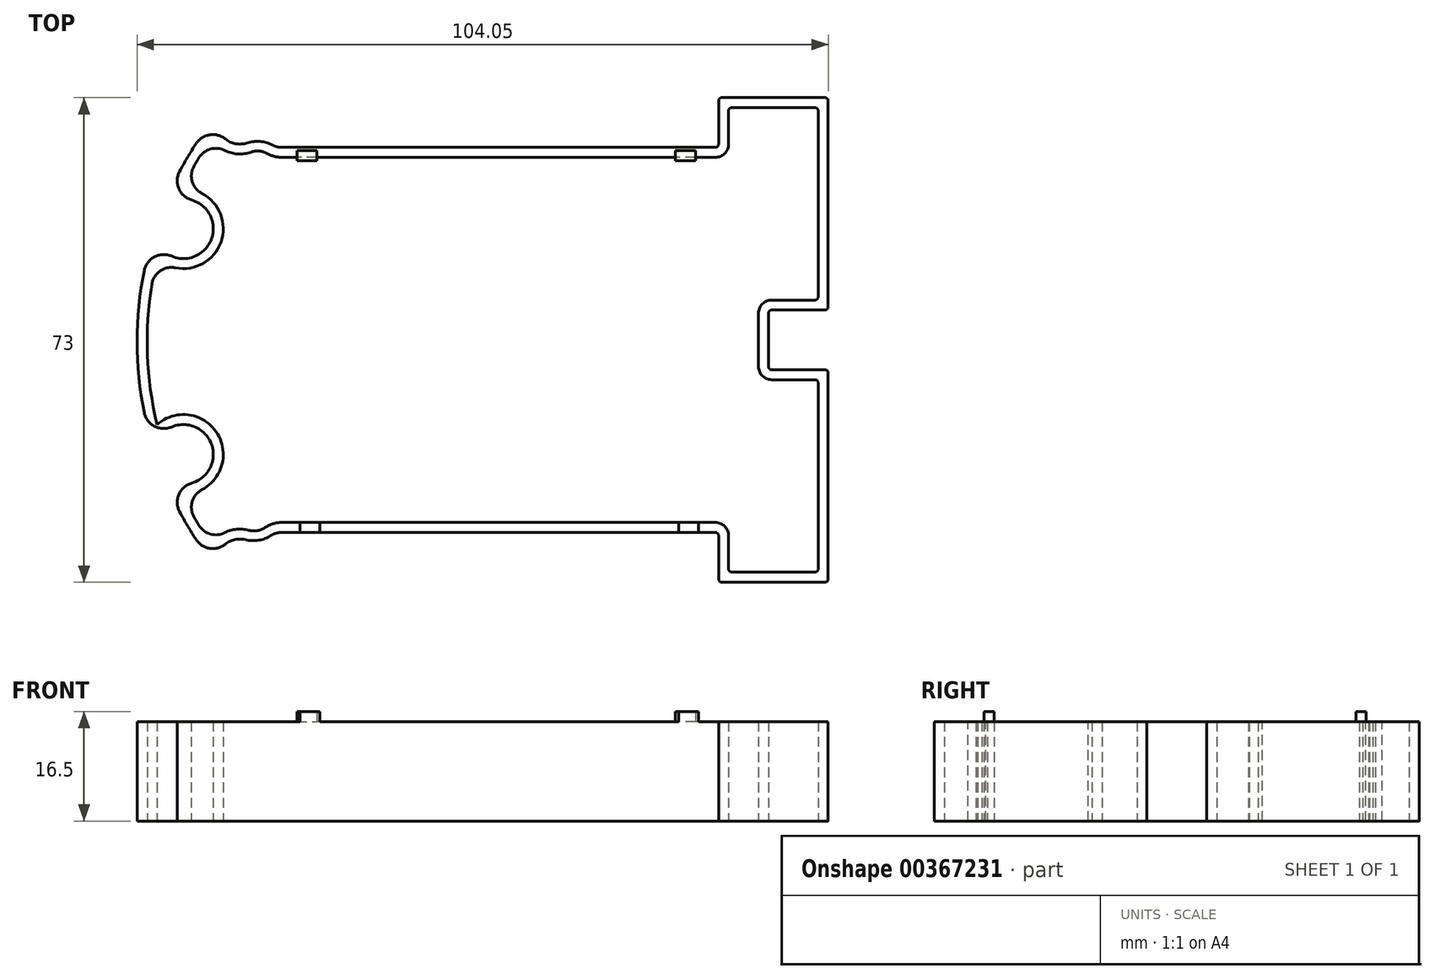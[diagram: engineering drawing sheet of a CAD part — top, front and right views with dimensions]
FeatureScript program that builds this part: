
annotation { "Feature Type Name" : "Feature", "Feature Type Description" : "" }
export const myFeature = defineFeature(function(context is Context, id is Id, definition is map)
    precondition{}
    {
        {
            var Q0;
            Q0=qCreatedBy(makeId("Top.planeOp"),FACE);
            var sketch = newSketch(context, id + "F0", { "sketchPlane" : qUnion([Q0])});
            skLineSegment(sketch, "E0.bottom", {"start": v(50.14, 35.5) * mm, "end": v(34.64, 35.5) * mm});
            skLineSegment(sketch, "E0.top", {"start": v(50.14, -37.5) * mm, "end": v(34.64, -37.5) * mm});
            skLineSegment(sketch, "E0.left", {"start": v(50.64, 35) * mm, "end": v(50.64, 4) * mm});
            skLineSegment(sketch, "E0.right", {"start": v(-53.4, -1.25) * mm, "end": v(-53.4, -1.25) * mm});
            skPoint(sketch, "E0.middle", {"position": v(-1.39, -1.25) * mm});
            skLineSegment(sketch, "E1.0", {"start": v(34.14, 35) * mm, "end": v(34.14, 28.5) * mm});
            skLineSegment(sketch, "E2.0", {"start": v(-34.64, 31) * mm, "end": v(-34.64, 30.87) * mm});
            skLineSegment(sketch, "E3.0", {"start": v(33.64, -30) * mm, "end": v(-31.64, -30) * mm});
            skLineSegment(sketch, "E4.0", {"start": v(33.64, 28) * mm, "end": v(-31.64, 28) * mm});
            skLineSegment(sketch, "E5", {"start": v(-1.39, -1.25) * mm, "end": v(-53.4, -1.25) * mm, "construction": true});
            skArc(sketch, "E6", {"start": v(-41.29, 33.04) * mm, "mid": v(-45.9, 26.36) * mm, "end": v(-49.48, 19.07) * mm});
            skPoint(sketch, "E7.orphan", {"position": v(-53.4, 35) * mm});
            skArc(sketch, "E8.filletArc", {"start": v(-33.03, 28.34) * mm, "mid": v(-32.35, 28.08) * mm, "end": v(-31.64, 28) * mm});
            skLineSegment(sketch, "E9", {"start": v(-34.64, -33.38) * mm, "end": v(-34.64, -33) * mm});
            skPoint(sketch, "E10.visualSharp", {"position": v(-34.64, -30) * mm});
            skArc(sketch, "E10.filletArc", {"start": v(-31.64, -30) * mm, "mid": v(-32.47, -30.12) * mm, "end": v(-33.24, -30.47) * mm});
            skLineSegment(sketch, "E11.trimOffspring", {"start": v(34.14, -30.5) * mm, "end": v(34.14, -37) * mm});
            skPoint(sketch, "E12.visualSharp", {"position": v(34.14, -30) * mm});
            skArc(sketch, "E12.filletArc", {"start": v(34.14, -30.5) * mm, "mid": v(34, -30.15) * mm, "end": v(33.64, -30) * mm});
            skPoint(sketch, "E13.visualSharp", {"position": v(34.14, -37.5) * mm});
            skArc(sketch, "E13.filletArc", {"start": v(34.14, -37) * mm, "mid": v(34.28, -37.36) * mm, "end": v(34.64, -37.5) * mm});
            skPoint(sketch, "E14.visualSharp", {"position": v(50.64, -37.5) * mm});
            skArc(sketch, "E14.filletArc", {"start": v(50.14, -37.5) * mm, "mid": v(50.5, -37.36) * mm, "end": v(50.64, -37) * mm});
            skPoint(sketch, "E15.visualSharp", {"position": v(50.64, 35.5) * mm});
            skArc(sketch, "E15.filletArc", {"start": v(50.64, 35) * mm, "mid": v(50.5, 35.35) * mm, "end": v(50.14, 35.5) * mm});
            skPoint(sketch, "E16.visualSharp", {"position": v(34.14, 35.5) * mm});
            skArc(sketch, "E16.filletArc", {"start": v(34.64, 35.5) * mm, "mid": v(34.28, 35.35) * mm, "end": v(34.14, 35) * mm});
            skPoint(sketch, "E17.visualSharp", {"position": v(34.14, 28) * mm});
            skArc(sketch, "E17.filletArc", {"start": v(33.64, 28) * mm, "mid": v(34, 28.14) * mm, "end": v(34.14, 28.5) * mm});
            skLineSegment(sketch, "E18", {"start": v(-34.64, 30.87) * mm, "end": v(-34.64, 31) * mm});
            skLineSegment(sketch, "E19", {"start": v(1.19, -1.25) * mm, "end": v(50.64, -1) * mm, "construction": true});
            skLineSegment(sketch, "E20.bottom", {"start": v(50.14, 3.5) * mm, "end": v(42.14, 3.5) * mm});
            skLineSegment(sketch, "E20.top", {"start": v(50.14, -5.5) * mm, "end": v(42.14, -5.5) * mm});
            skLineSegment(sketch, "E20.right", {"start": v(41.64, 3) * mm, "end": v(41.64, -5) * mm});
            skLineSegment(sketch, "E21.trimOffspring", {"start": v(50.64, -6) * mm, "end": v(50.64, -37) * mm});
            skLineSegment(sketch, "E22", {"start": v(-37.95, 32) * mm, "end": v(-37.95, -34.5) * mm, "construction": true});
            skArc(sketch, "E23", {"start": v(-41.29, 33.04) * mm, "mid": v(-40.41, 29.51) * mm, "end": v(-36.88, 28.66) * mm});
            skArc(sketch, "E24", {"start": v(-37.11, -31.1) * mm, "mid": v(-40.5, -32.1) * mm, "end": v(-41.29, -35.55) * mm});
            skLineSegment(sketch, "E25.0", {"start": v(-0.88, 15.75) * mm, "end": v(-50.95, 15.75) * mm, "construction": true});
            skLineSegment(sketch, "E26.0", {"start": v(-1.9, -18.25) * mm, "end": v(-53.9, -18.25) * mm, "construction": true});
            skLineSegment(sketch, "E27.0", {"start": v(-46.45, 35) * mm, "end": v(-46.45, -37.5) * mm, "construction": true});
            skArc(sketch, "E28", {"start": v(-50.9, 15.1) * mm, "mid": v(-42.21, 14.23) * mm, "end": v(-49.48, 19.07) * mm});
            skArc(sketch, "E29", {"start": v(-49.48, -21.58) * mm, "mid": v(-42.21, -16.74) * mm, "end": v(-50.9, -17.6) * mm});
            skPoint(sketch, "E30.visualSharp", {"position": v(50.64, -5.5) * mm});
            skArc(sketch, "E30.filletArc", {"start": v(50.64, -6) * mm, "mid": v(50.5, -5.65) * mm, "end": v(50.14, -5.5) * mm});
            skPoint(sketch, "E31.visualSharp", {"position": v(41.64, -5.5) * mm});
            skArc(sketch, "E31.filletArc", {"start": v(41.64, -5) * mm, "mid": v(41.78, -5.36) * mm, "end": v(42.14, -5.5) * mm});
            skPoint(sketch, "E32.visualSharp", {"position": v(41.64, 3.5) * mm});
            skArc(sketch, "E32.filletArc", {"start": v(42.14, 3.5) * mm, "mid": v(41.78, 3.35) * mm, "end": v(41.64, 3) * mm});
            skPoint(sketch, "E33.visualSharp", {"position": v(50.64, 3.5) * mm});
            skArc(sketch, "E33.filletArc", {"start": v(50.14, 3.5) * mm, "mid": v(50.5, 3.64) * mm, "end": v(50.64, 4) * mm});
            skArc(sketch, "E34.0", {"start": v(-31.64, -28.5) * mm, "mid": v(-33.65, -28.98) * mm, "end": v(-35.24, -30.3) * mm});
            skLineSegment(sketch, "E35.0", {"start": v(33.64, -28.5) * mm, "end": v(-31.64, -28.5) * mm});
            skLineSegment(sketch, "E36.0", {"start": v(35.64, -30) * mm, "end": v(35.64, -35.5) * mm});
            skLineSegment(sketch, "E37.0", {"start": v(48.64, -36) * mm, "end": v(36.14, -36) * mm});
            skArc(sketch, "E38.0", {"start": v(35.64, -30.5) * mm, "mid": v(35.05, -29.09) * mm, "end": v(33.64, -28.5) * mm});
            skArc(sketch, "E39.filletArc", {"start": v(35.64, -35.5) * mm, "mid": v(35.78, -35.86) * mm, "end": v(36.14, -36) * mm});
            skLineSegment(sketch, "E40.0", {"start": v(49.14, -7.5) * mm, "end": v(49.14, -35.5) * mm});
            skLineSegment(sketch, "E41.0", {"start": v(49.14, 33.5) * mm, "end": v(49.14, 5.5) * mm});
            skLineSegment(sketch, "E42.0", {"start": v(48.64, 5) * mm, "end": v(42.14, 5) * mm});
            skLineSegment(sketch, "E43.0", {"start": v(40.14, 3) * mm, "end": v(40.14, -5) * mm});
            skLineSegment(sketch, "E44.0", {"start": v(48.64, -7) * mm, "end": v(42.14, -7) * mm});
            skArc(sketch, "E45.0", {"start": v(42.14, 5) * mm, "mid": v(40.72, 4.41) * mm, "end": v(40.14, 3) * mm});
            skArc(sketch, "E46.0", {"start": v(40.14, -5) * mm, "mid": v(40.72, -6.42) * mm, "end": v(42.14, -7) * mm});
            skArc(sketch, "E47.filletArc", {"start": v(48.64, 5) * mm, "mid": v(49, 5.14) * mm, "end": v(49.14, 5.5) * mm});
            skArc(sketch, "E48.filletArc", {"start": v(49.14, -7.5) * mm, "mid": v(49, -7.15) * mm, "end": v(48.64, -7) * mm});
            skArc(sketch, "E49.filletArc", {"start": v(48.64, -36) * mm, "mid": v(49, -35.86) * mm, "end": v(49.14, -35.5) * mm});
            skLineSegment(sketch, "E50.0", {"start": v(48.64, 34) * mm, "end": v(36.14, 34) * mm});
            skLineSegment(sketch, "E51.0", {"start": v(35.64, 33.5) * mm, "end": v(35.64, 28.5) * mm});
            skLineSegment(sketch, "E52.0", {"start": v(33.64, 26.5) * mm, "end": v(-31.64, 26.5) * mm});
            skArc(sketch, "E53.0", {"start": v(-34.97, 27.98) * mm, "mid": v(-33.46, 26.88) * mm, "end": v(-31.64, 26.5) * mm});
            skArc(sketch, "E54.0", {"start": v(-42.2, 29.36) * mm, "mid": v(-38.89, 27.08) * mm, "end": v(-34.97, 27.98) * mm});
            skArc(sketch, "E55.0", {"start": v(-42.2, 29.36) * mm, "mid": v(-44.6, 25.64) * mm, "end": v(-46.67, 21.74) * mm});
            skArc(sketch, "E56.0", {"start": v(-50.42, 11.24) * mm, "mid": v(-40.8, 13.73) * mm, "end": v(-46.67, 21.74) * mm});
            skArc(sketch, "E57.0", {"start": v(-46.67, -24.25) * mm, "mid": v(-40.8, -16.24) * mm, "end": v(-50.42, -13.75) * mm});
            skArc(sketch, "E58.0", {"start": v(-35.24, -30.3) * mm, "mid": v(-39.04, -29.63) * mm, "end": v(-42.2, -31.86) * mm});
            skArc(sketch, "E59.0", {"start": v(33.64, 26.5) * mm, "mid": v(35.05, 27.08) * mm, "end": v(35.64, 28.5) * mm});
            skArc(sketch, "E60.filletArc", {"start": v(36.14, 34) * mm, "mid": v(35.78, 33.85) * mm, "end": v(35.64, 33.5) * mm});
            skArc(sketch, "E61.filletArc", {"start": v(49.14, 33.5) * mm, "mid": v(49, 33.85) * mm, "end": v(48.64, 34) * mm});
            skArc(sketch, "E62.trimOffspring", {"start": v(-50.42, 11.24) * mm, "mid": v(-51.9, -1.25) * mm, "end": v(-50.42, -13.75) * mm});
            skArc(sketch, "E63.trimOffspring", {"start": v(-50.9, 15.1) * mm, "mid": v(-53.4, -1.25) * mm, "end": v(-50.9, -17.6) * mm});
            skArc(sketch, "E64.trimOffspring", {"start": v(-49.48, -21.58) * mm, "mid": v(-45.9, -28.87) * mm, "end": v(-41.29, -35.55) * mm});
            skArc(sketch, "E65.trimOffspring", {"start": v(-46.67, -24.25) * mm, "mid": v(-44.6, -28.15) * mm, "end": v(-42.2, -31.86) * mm});
            skArc(sketch, "E66.filletArc", {"start": v(-37.11, -31.1) * mm, "mid": v(-35.11, -31.18) * mm, "end": v(-33.24, -30.47) * mm});
            skArc(sketch, "E67.filletArc", {"start": v(-33.03, 28.34) * mm, "mid": v(-34.92, 28.89) * mm, "end": v(-36.88, 28.66) * mm});
            skSolve(sketch);
        }
        {
            var Q0;
            Q0=makeQuery(id+"F0.imprint","IMPRINT",FACE,{"disambiguationData":[TD([[makeQuery(id+"F0.imprint","IMPRINT",EDGE,{"derivedFrom":sQuery(id+"F0.wireOp",EDGE,"E0.bottom")}),1.0]])]});
            extrude(context, id + "F1", {"entities" : qUnion([Q0]), "depth" : 15 * mm});
        }
        {
            var Q0;
            Q0=makeQuery(id+"F1.opExtrude","SWEPT_EDGE",EDGE,{"disambiguationData":[OSD([sQuery(id+"F0.wireOp",EDGE,"E24"),sQuery(id+"F0.wireOp",EDGE,"E64.trimOffspring")])]});
            var Q1;
            Q1=makeQuery(id+"F1.opExtrude","SWEPT_EDGE",EDGE,{"disambiguationData":[OSD([sQuery(id+"F0.wireOp",EDGE,"E29"),sQuery(id+"F0.wireOp",EDGE,"E63.trimOffspring")])]});
            var Q2;
            Q2=makeQuery(id+"F1.opExtrude","SWEPT_EDGE",EDGE,{"disambiguationData":[OSD([sQuery(id+"F0.wireOp",EDGE,"E29"),sQuery(id+"F0.wireOp",EDGE,"E64.trimOffspring")])]});
            var Q3;
            Q3=makeQuery(id+"F1.opExtrude","SWEPT_EDGE",EDGE,{"disambiguationData":[OSD([sQuery(id+"F0.wireOp",EDGE,"E57.0"),sQuery(id+"F0.wireOp",EDGE,"E65.trimOffspring")])]});
            var Q4;
            Q4=makeQuery(id+"F1.opExtrude","SWEPT_EDGE",EDGE,{"disambiguationData":[OSD([sQuery(id+"F0.wireOp",EDGE,"E58.0"),sQuery(id+"F0.wireOp",EDGE,"E65.trimOffspring")])]});
            var Q5;
            Q5=makeQuery(id+"F1.opExtrude","SWEPT_EDGE",EDGE,{"disambiguationData":[OSD([sQuery(id+"F0.wireOp",EDGE,"E28"),sQuery(id+"F0.wireOp",EDGE,"E63.trimOffspring")])]});
            var Q6;
            Q6=makeQuery(id+"F1.opExtrude","SWEPT_EDGE",EDGE,{"disambiguationData":[OSD([sQuery(id+"F0.wireOp",EDGE,"E6"),sQuery(id+"F0.wireOp",EDGE,"E28")])]});
            var Q7;
            Q7=makeQuery(id+"F1.opExtrude","SWEPT_EDGE",EDGE,{"disambiguationData":[OSD([sQuery(id+"F0.wireOp",EDGE,"E56.0"),sQuery(id+"F0.wireOp",EDGE,"E62.trimOffspring")])]});
            var Q8;
            Q8=makeQuery(id+"F1.opExtrude","SWEPT_EDGE",EDGE,{"disambiguationData":[OSD([sQuery(id+"F0.wireOp",EDGE,"E55.0"),sQuery(id+"F0.wireOp",EDGE,"E56.0")])]});
            var Q9;
            Q9=makeQuery(id+"F1.opExtrude","SWEPT_EDGE",EDGE,{"disambiguationData":[OSD([sQuery(id+"F0.wireOp",EDGE,"E54.0"),sQuery(id+"F0.wireOp",EDGE,"E55.0")])]});
            var Q10;
            Q10=makeQuery(id+"F1.opExtrude","SWEPT_EDGE",EDGE,{"disambiguationData":[OSD([sQuery(id+"F0.wireOp",EDGE,"E6"),sQuery(id+"F0.wireOp",EDGE,"E23")])]});
            var Q11;
            Q11=makeQuery(id+"F1.opExtrude","SWEPT_EDGE",EDGE,{"disambiguationData":[OSD([sQuery(id+"F0.wireOp",EDGE,"E53.0"),sQuery(id+"F0.wireOp",EDGE,"E54.0")])]});
            var Q12;
            Q12=makeQuery(id+"F1.opExtrude","SWEPT_EDGE",EDGE,{"disambiguationData":[OSD([sQuery(id+"F0.wireOp",EDGE,"E34.0"),sQuery(id+"F0.wireOp",EDGE,"E58.0")])]});
            fillet(context, id + "F2", {"entities" : qUnion([Q0, Q1, Q2, Q3, Q4, Q5, Q6, Q7, Q8, Q9, Q10, Q11, Q12]), "radius" : 3 * mm, "tangentPropagation" : true, "allowEdgeOverflow" : false});
        }
        {
            var Q0;
            Q0=makeQuery(id+"F1.opExtrude","CAP_FACE",FACE,{"disambiguationData":[OSD([sQuery(id+"F0.wireOp",EDGE,"E0.bottom"),sQuery(id+"F0.wireOp",EDGE,"E0.top"),sQuery(id+"F0.wireOp",EDGE,"E0.left"),sQuery(id+"F0.wireOp",EDGE,"E1.0"),sQuery(id+"F0.wireOp",EDGE,"E3.0"),sQuery(id+"F0.wireOp",EDGE,"E4.0"),sQuery(id+"F0.wireOp",EDGE,"E6"),sQuery(id+"F0.wireOp",EDGE,"E8.filletArc"),sQuery(id+"F0.wireOp",EDGE,"E9"),sQuery(id+"F0.wireOp",EDGE,"E10.filletArc"),sQuery(id+"F0.wireOp",EDGE,"E11.trimOffspring"),sQuery(id+"F0.wireOp",EDGE,"E12.filletArc"),sQuery(id+"F0.wireOp",EDGE,"E13.filletArc"),sQuery(id+"F0.wireOp",EDGE,"E14.filletArc"),sQuery(id+"F0.wireOp",EDGE,"E15.filletArc"),sQuery(id+"F0.wireOp",EDGE,"E16.filletArc"),sQuery(id+"F0.wireOp",EDGE,"E17.filletArc"),sQuery(id+"F0.wireOp",EDGE,"E18"),sQuery(id+"F0.wireOp",EDGE,"E20.bottom"),sQuery(id+"F0.wireOp",EDGE,"E20.top"),sQuery(id+"F0.wireOp",EDGE,"E20.right"),sQuery(id+"F0.wireOp",EDGE,"E21.trimOffspring"),sQuery(id+"F0.wireOp",EDGE,"E23"),sQuery(id+"F0.wireOp",EDGE,"E24"),sQuery(id+"F0.wireOp",EDGE,"E28"),sQuery(id+"F0.wireOp",EDGE,"E29"),sQuery(id+"F0.wireOp",EDGE,"E30.filletArc"),sQuery(id+"F0.wireOp",EDGE,"E31.filletArc"),sQuery(id+"F0.wireOp",EDGE,"E32.filletArc"),sQuery(id+"F0.wireOp",EDGE,"E33.filletArc"),sQuery(id+"F0.wireOp",EDGE,"E34.0"),sQuery(id+"F0.wireOp",EDGE,"E35.0"),sQuery(id+"F0.wireOp",EDGE,"E36.0"),sQuery(id+"F0.wireOp",EDGE,"E37.0"),sQuery(id+"F0.wireOp",EDGE,"E38.0"),sQuery(id+"F0.wireOp",EDGE,"E39.filletArc"),sQuery(id+"F0.wireOp",EDGE,"E40.0"),sQuery(id+"F0.wireOp",EDGE,"E41.0"),sQuery(id+"F0.wireOp",EDGE,"E42.0"),sQuery(id+"F0.wireOp",EDGE,"E43.0"),sQuery(id+"F0.wireOp",EDGE,"E44.0"),sQuery(id+"F0.wireOp",EDGE,"E45.0"),sQuery(id+"F0.wireOp",EDGE,"E46.0"),sQuery(id+"F0.wireOp",EDGE,"E47.filletArc"),sQuery(id+"F0.wireOp",EDGE,"E48.filletArc"),sQuery(id+"F0.wireOp",EDGE,"E49.filletArc"),sQuery(id+"F0.wireOp",EDGE,"E50.0"),sQuery(id+"F0.wireOp",EDGE,"E51.0"),sQuery(id+"F0.wireOp",EDGE,"E52.0"),sQuery(id+"F0.wireOp",EDGE,"E53.0"),sQuery(id+"F0.wireOp",EDGE,"E54.0"),sQuery(id+"F0.wireOp",EDGE,"E55.0"),sQuery(id+"F0.wireOp",EDGE,"E56.0"),sQuery(id+"F0.wireOp",EDGE,"E57.0"),sQuery(id+"F0.wireOp",EDGE,"E58.0"),sQuery(id+"F0.wireOp",EDGE,"E59.0"),sQuery(id+"F0.wireOp",EDGE,"E60.filletArc"),sQuery(id+"F0.wireOp",EDGE,"E61.filletArc"),sQuery(id+"F0.wireOp",EDGE,"E62.trimOffspring"),sQuery(id+"F0.wireOp",EDGE,"E63.trimOffspring"),sQuery(id+"F0.wireOp",EDGE,"E64.trimOffspring"),sQuery(id+"F0.wireOp",EDGE,"E65.trimOffspring")])],"isStart":false});
            var sketch = newSketch(context, id + "F3", { "sketchPlane" : qUnion([Q0])});
            skLineSegment(sketch, "E68.0", {"start": v(31.12, -5.75) * mm, "end": v(31.12, -37) * mm, "construction": true});
            skLineSegment(sketch, "E69.0", {"start": v(30.64, 34.5) * mm, "end": v(30.64, 3.25) * mm, "construction": true});
            skLineSegment(sketch, "E70.0", {"start": v(-29.36, 34.5) * mm, "end": v(-29.36, 3.25) * mm, "construction": true});
            skLineSegment(sketch, "E71.0", {"start": v(-28.88, -5.75) * mm, "end": v(-28.88, -37) * mm, "construction": true});
            skLineSegment(sketch, "E72.0", {"start": v(34.12, -28.5) * mm, "end": v(-31.13, -28.5) * mm, "construction": true});
            skLineSegment(sketch, "E73.0", {"start": v(33.64, 26) * mm, "end": v(-31.61, 26) * mm, "construction": true});
            skLineSegment(sketch, "E74.bottom", {"start": v(31.12, -30) * mm, "end": v(28.12, -30) * mm});
            skLineSegment(sketch, "E74.top", {"start": v(31.12, -28.5) * mm, "end": v(28.12, -28.5) * mm});
            skLineSegment(sketch, "E74.left", {"start": v(31.12, -30) * mm, "end": v(31.12, -28.5) * mm});
            skLineSegment(sketch, "E74.right", {"start": v(28.12, -30) * mm, "end": v(28.12, -28.5) * mm});
            skLineSegment(sketch, "E75.bottom", {"start": v(-28.88, -30) * mm, "end": v(-25.88, -30) * mm});
            skLineSegment(sketch, "E75.top", {"start": v(-28.88, -28.5) * mm, "end": v(-25.88, -28.5) * mm});
            skLineSegment(sketch, "E75.left", {"start": v(-28.88, -30) * mm, "end": v(-28.88, -28.5) * mm});
            skLineSegment(sketch, "E75.right", {"start": v(-25.88, -30) * mm, "end": v(-25.88, -28.5) * mm});
            skLineSegment(sketch, "E76.bottom", {"start": v(30.64, 26) * mm, "end": v(27.64, 26) * mm});
            skLineSegment(sketch, "E76.top", {"start": v(30.64, 27.5) * mm, "end": v(27.64, 27.5) * mm});
            skLineSegment(sketch, "E76.left", {"start": v(30.64, 26) * mm, "end": v(30.64, 27.5) * mm});
            skLineSegment(sketch, "E76.right", {"start": v(27.64, 26) * mm, "end": v(27.64, 27.5) * mm});
            skLineSegment(sketch, "E77.bottom", {"start": v(-29.36, 26) * mm, "end": v(-26.36, 26) * mm});
            skLineSegment(sketch, "E77.top", {"start": v(-29.36, 27.5) * mm, "end": v(-26.36, 27.5) * mm});
            skLineSegment(sketch, "E77.left", {"start": v(-29.36, 26) * mm, "end": v(-29.36, 27.5) * mm});
            skLineSegment(sketch, "E77.right", {"start": v(-26.36, 26) * mm, "end": v(-26.36, 27.5) * mm});
            skSolve(sketch);
        }
        {
            var Q0;
            Q0 = qSketchRegion(id + "F3", true);
            extrude(context, id + "F4", {"entities" : qUnion([Q0]), "operationType" : NewBodyOperationType.ADD, "depth" : 1.5 * mm});
        }
    });
